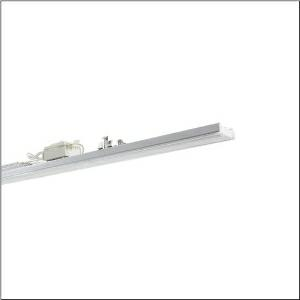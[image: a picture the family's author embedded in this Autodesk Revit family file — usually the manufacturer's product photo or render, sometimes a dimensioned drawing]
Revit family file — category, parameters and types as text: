
# Revit family: licross_r__11_recessed_ho_51tl12dn4exm3s4_9bea
name_source: partatom
category: Lighting Fixtures
units: mm (PartAtom-declared; Revit-internal decimal feet)

## family parameters
Cut with Voids When Loaded = No
Host = Face
Light Source = No
Part Type = Normal
Room Calculation Point = No
Round Connector Dimension = Use Diameter
Shared = No

## types (1)
- --- (1 x LED, 1000 lm, 7.2 W, 4000K)
    Apparent Load = 7 VA
    CIE Flux Codes = 66 91 98 100 100
    Color Rendering = 80
    Color Temperature = 4000K
    Default Elevation = 1800 mm
    Description = Licross® 11 Recessed HO, luminaire insert, of sheet steel, coil coated, white, length: 1.500mm, width: 66mm, height: 67mm, LED rated luminous flux: 14.030lm, light colour: 840, control gear: DALI 2, with plug, 6-pole, with phase selection, for trunking rail, 9 or 11-core, mains connection: 220..240V, AC, 50/60Hz, rated input power: 81W, for trunking rail, 9-/11-core, internal wiring halogen-free, for emergency light function, converter,control gear: single battery element, battery: LiFePO4, 9Ah, primary optical cover: cover, of PMMA, light emission: direct distribution, primary light characteristic: symmetric, protection rating (complete): IP40, insulation class (complete): insulation class I (protective earthing), certification: CE, UKCA, protection symbol: D if used in an environment without relevant dust loads with corresponding accessories, impact resistance: IK06, permissible ambient temperature for indoor applications: +5..+30°C, standard: EN 60598-2-22, LABS conformity tested according to VDMA 24364:2018-05, reducing of maximum allowable ambient temperature of 5°C with ceiling mounting, corresponds to IFS (International Featured Standards) requirements for safety and quality in the food industry, packaging unit: 1 piece
    Height = 58 mm
    Lamp = 1 x LED
    Lamp Light Flux = 1000 lm
    Lamp Power = 7.2 W
    Lamp count = 1
    Length = 1500 mm
    Luminous efficacy = 139 lm/W
    Manufacturer = Siteco
    ModVariant = No
    Model = 51TL12DN4EXM3S4
    Mounting Place = Ceiling
    Mounting Type = Pendant
    Number of Poles = 1
    OnlyDefault = Yes
    Power Factor = 1
    Product Name = Licross® 11 Recessed HO
    Product group = luminaire insert | ceiling pendant
    ProductGroupID = 902
    Protection Class = Protection class I
    Protection Degree = IP 40
    RLX_Detail_Level = 1
    RLX_Emergency_Light_Flux = 0 lm
    RLX_Emergency_Type = 0
    RLX_Emergency_Type_DB = No
    RlxData = <blob elided: 24969 chars, md5=3411d26d>
    Socket = socket
    Standby Power = 0 W
    System Light Flux = 1000 lm
    System Power = 7 W
    Type Comments = : emergency light operation: 3 h
    Type Image = l_1296930.jpg
    URL = http://relux.com
    VarID = @adj_111419
    Voltage = 0 V
    Weight = 0.00 kg
    Width = 66 mm

## geometry (parser evidence)
native form markers: Blend x4, Sweep x10
no freeform markers — native parametric forms only
